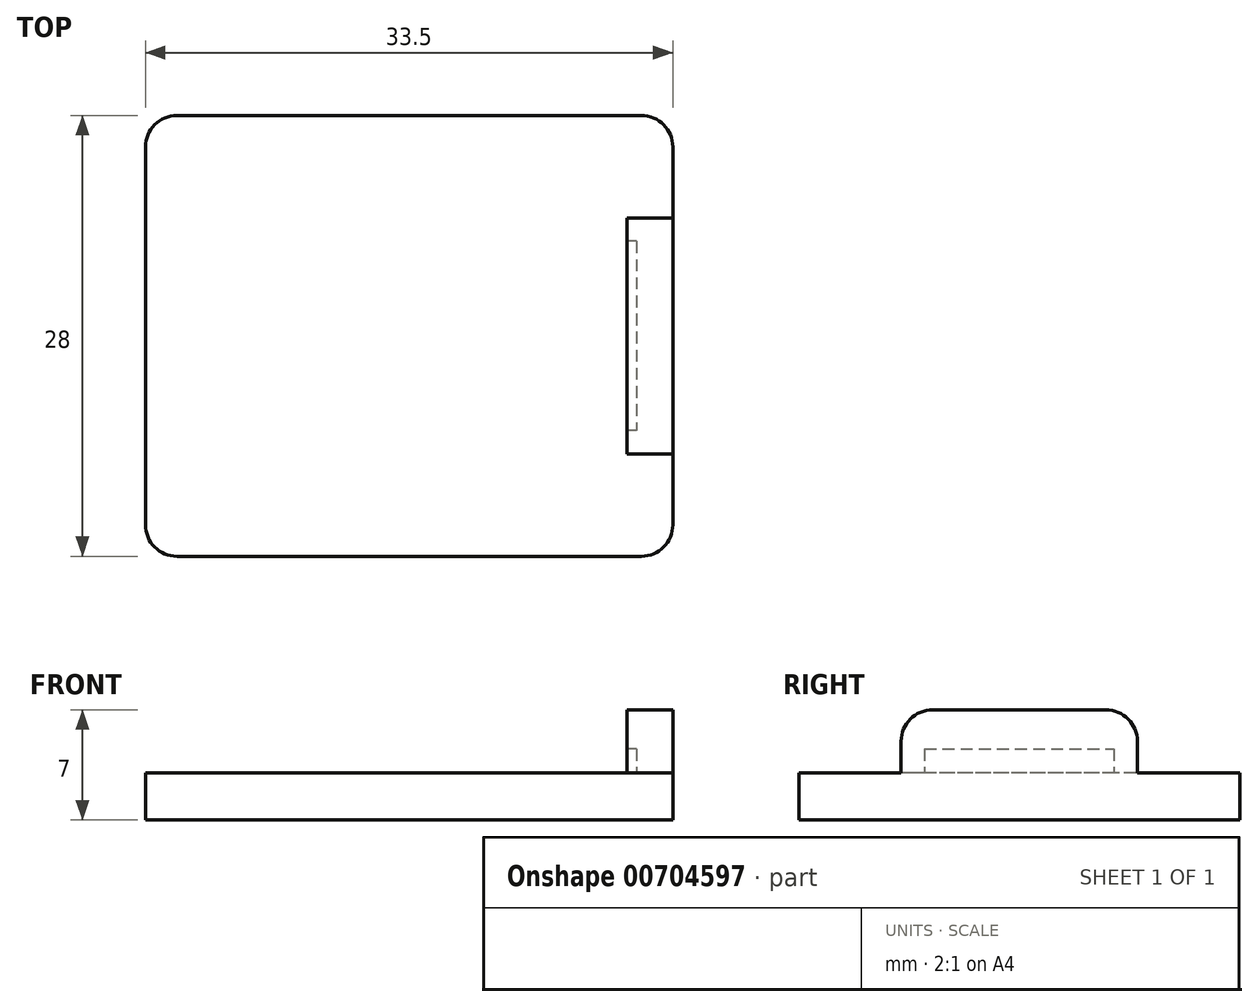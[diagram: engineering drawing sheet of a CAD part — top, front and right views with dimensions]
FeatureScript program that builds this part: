
annotation { "Feature Type Name" : "Feature", "Feature Type Description" : "" }
export const myFeature = defineFeature(function(context is Context, id is Id, definition is map)
    precondition{}
    {
        {
            var Q0;
            Q0=qCreatedBy(makeId("Top.planeOp"),FACE);
            var sketch = newSketch(context, id + "F0", { "sketchPlane" : qUnion([Q0])});
            skLineSegment(sketch, "E0.bottom", {"start": v(16.75, 14) * mm, "end": v(-16.75, 14) * mm});
            skLineSegment(sketch, "E0.top", {"start": v(16.75, -14) * mm, "end": v(-16.75, -14) * mm});
            skLineSegment(sketch, "E0.left", {"start": v(16.75, 14) * mm, "end": v(16.75, -14) * mm});
            skLineSegment(sketch, "E0.right", {"start": v(-16.75, 14) * mm, "end": v(-16.75, -14) * mm});
            skPoint(sketch, "E0.middle", {"position": v(0, 0) * mm});
            skSolve(sketch);
        }
        {
            var Q0;
            Q0=makeQuery(id+"F0.imprint","IMPRINT",FACE,{"disambiguationData":[TD([[makeQuery(id+"F0.imprint","IMPRINT",EDGE,{"derivedFrom":sQuery(id+"F0.wireOp",EDGE,"E0.bottom")}),1.0]])]});
            extrude(context, id + "F1", {"entities" : qUnion([Q0]), "depth" : 3 * mm, "offsetDistance" : 25 * mm});
        }
        {
            var Q0;
            Q0=makeQuery(id+"F1.opExtrude","SWEPT_EDGE",EDGE,{"disambiguationData":[OSD([sQuery(id+"F0.wireOp",EDGE,"E0.top"),sQuery(id+"F0.wireOp",EDGE,"E0.right")])]});
            var Q1;
            Q1=makeQuery(id+"F1.opExtrude","SWEPT_EDGE",EDGE,{"disambiguationData":[OSD([sQuery(id+"F0.wireOp",EDGE,"E0.top"),sQuery(id+"F0.wireOp",EDGE,"E0.left")])]});
            var Q2;
            Q2=makeQuery(id+"F1.opExtrude","SWEPT_EDGE",EDGE,{"disambiguationData":[OSD([sQuery(id+"F0.wireOp",EDGE,"E0.bottom"),sQuery(id+"F0.wireOp",EDGE,"E0.left")])]});
            var Q3;
            Q3=makeQuery(id+"F1.opExtrude","SWEPT_EDGE",EDGE,{"disambiguationData":[OSD([sQuery(id+"F0.wireOp",EDGE,"E0.bottom"),sQuery(id+"F0.wireOp",EDGE,"E0.right")])]});
            fillet(context, id + "F2", {"entities" : qUnion([Q0, Q1, Q2, Q3]), "radius" : 2 * mm, "tangentPropagation" : true, "allowEdgeOverflow" : false});
        }
        {
            var Q0;
            Q0=makeQuery(id+"F1.opExtrude","CAP_FACE",FACE,{"disambiguationData":[OSD([sQuery(id+"F0.wireOp",EDGE,"E0.bottom"),sQuery(id+"F0.wireOp",EDGE,"E0.top"),sQuery(id+"F0.wireOp",EDGE,"E0.left"),sQuery(id+"F0.wireOp",EDGE,"E0.right")])],"isStart":false});
            var sketch = newSketch(context, id + "F3", { "sketchPlane" : qUnion([Q0])});
            skLineSegment(sketch, "E1.bottom", {"start": v(16.75, 7.5) * mm, "end": v(13.85, 7.5) * mm});
            skLineSegment(sketch, "E1.top", {"start": v(16.75, -7.5) * mm, "end": v(13.85, -7.5) * mm});
            skLineSegment(sketch, "E1.left", {"start": v(16.75, 7.5) * mm, "end": v(16.75, -7.5) * mm});
            skLineSegment(sketch, "E1.right", {"start": v(13.85, 7.5) * mm, "end": v(13.85, -7.5) * mm});
            skPoint(sketch, "E1.middle", {"position": v(15.3, 0) * mm});
            skPoint(sketch, "E2", {"position": v(16.75, 0) * mm});
            skSolve(sketch);
        }
        {
            var Q0;
            Q0=makeQuery(id+"F3.imprint","IMPRINT",FACE,{"disambiguationData":[TD([[makeQuery(id+"F3.imprint","IMPRINT",EDGE,{"derivedFrom":sQuery(id+"F3.wireOp",EDGE,"E1.bottom")}),1.0]])]});
            extrude(context, id + "F4", {"entities" : qUnion([Q0]), "operationType" : NewBodyOperationType.ADD, "depth" : 4 * mm, "offsetDistance" : 25 * mm});
        }
        {
            var Q0;
            Q0=makeQuery(id+"F4.opExtrude","SWEPT_FACE",FACE,{"disambiguationData":[OSD([sQuery(id+"F3.wireOp",EDGE,"E1.right")])]});
            var sketch = newSketch(context, id + "F5", { "sketchPlane" : qUnion([Q0])});
            skLineSegment(sketch, "E3.bottom", {"start": v(6.01, 4.5) * mm, "end": v(-6.02, 4.51) * mm});
            skLineSegment(sketch, "E3.top", {"start": v(6.01, 3) * mm, "end": v(-6.02, 3) * mm});
            skLineSegment(sketch, "E3.left", {"start": v(6.01, 4.5) * mm, "end": v(6.01, 3) * mm});
            skLineSegment(sketch, "E3.right", {"start": v(-6.02, 4.5) * mm, "end": v(-6.02, 3) * mm});
            skPoint(sketch, "E3.middle", {"position": v(0, 3.76) * mm});
            skPoint(sketch, "E3.middle.positionSnap0", {"position": v(0, 3) * mm});
            skPoint(sketch, "E3.centerSnap0", {"position": v(0, 3) * mm});
            skSolve(sketch);
        }
        {
            var Q0;
            Q0=makeQuery(id+"F5.imprint","IMPRINT",FACE,{"disambiguationData":[TD([[makeQuery(id+"F5.imprint","IMPRINT",EDGE,{"derivedFrom":sQuery(id+"F5.wireOp",EDGE,"E3.bottom")}),1.0]])]});
            extrude(context, id + "F6", {"entities" : qUnion([Q0]), "operationType" : NewBodyOperationType.REMOVE, "oppositeDirection" : true, "depth" : 0.6 * mm, "offsetDistance" : 25 * mm});
        }
        {
            var Q0;
            Q0=makeQuery(id+"F4.opExtrude","CAP_EDGE",EDGE,{"disambiguationData":[OSD([sQuery(id+"F3.wireOp",EDGE,"E1.bottom")])],"isStart":false});
            var Q1;
            Q1=makeQuery(id+"F4.opExtrude","CAP_EDGE",EDGE,{"disambiguationData":[OSD([sQuery(id+"F3.wireOp",EDGE,"E1.top")])],"isStart":false});
            fillet(context, id + "F7", {"entities" : qUnion([Q0, Q1]), "radius" : 2 * mm, "tangentPropagation" : true, "allowEdgeOverflow" : false});
        }
    });
